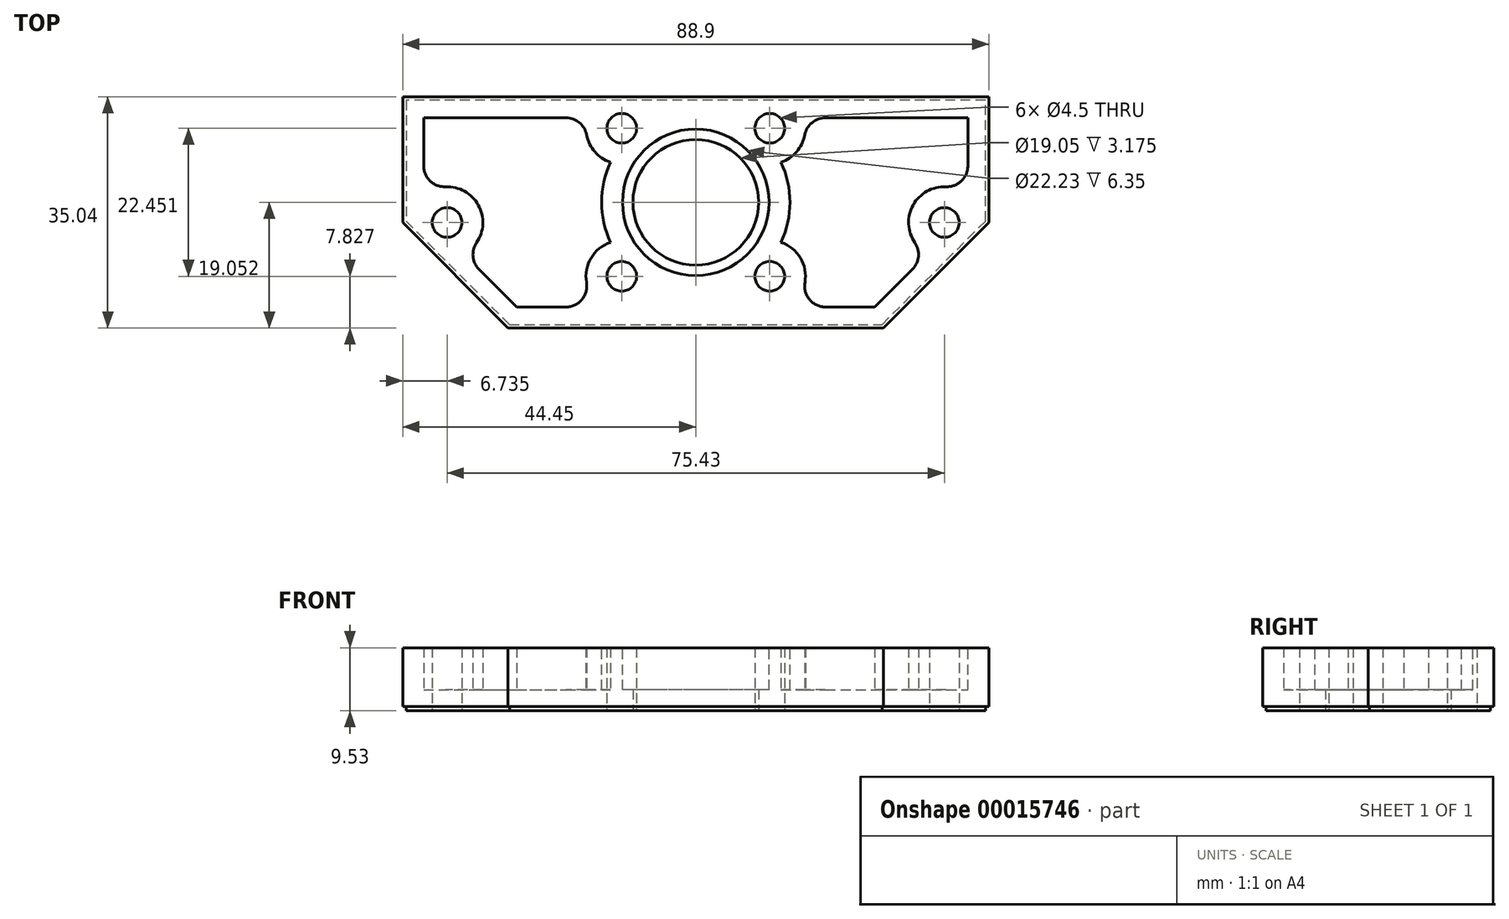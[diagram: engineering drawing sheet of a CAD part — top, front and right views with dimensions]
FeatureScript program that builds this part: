
annotation { "Feature Type Name" : "Feature", "Feature Type Description" : "" }
export const myFeature = defineFeature(function(context is Context, id is Id, definition is map)
    precondition{}
    {
        {
            var Q0;
            Q0=qCreatedBy(makeId("Top.planeOp"),FACE);
            var sketch = newSketch(context, id + "F0", { "sketchPlane" : qUnion([Q0])});
            skLineSegment(sketch, "E0.bottom", {"start": v(0, 0) * mm, "end": v(88.9, 0) * mm});
            skLineSegment(sketch, "E0.left", {"start": v(0, 0) * mm, "end": v(0, -19.05) * mm});
            skLineSegment(sketch, "E0.right", {"start": v(88.9, 0) * mm, "end": v(88.9, -19.05) * mm});
            skLineSegment(sketch, "E1", {"start": v(0, -19.05) * mm, "end": v(15.99, -35.04) * mm});
            skLineSegment(sketch, "E2", {"start": v(88.9, -19.05) * mm, "end": v(72.91, -35.04) * mm});
            skLineSegment(sketch, "E3", {"start": v(15.99, -35.04) * mm, "end": v(72.91, -35.04) * mm});
            skLineSegment(sketch, "E4", {"start": v(0, -19.05) * mm, "end": v(6.74, -19.05) * mm, "construction": true});
            skCircle(sketch, "E5", {"center": v(6.74, -19.05) * mm, "radius": 4.76 * mm, "construction": true});
            skLineSegment(sketch, "E6", {"start": v(88.9, -19.05) * mm, "end": v(82.16, -19.05) * mm, "construction": true});
            skLineSegment(sketch, "E7", {"start": v(44.45, -15.99) * mm, "end": v(44.45, -35.04) * mm, "construction": true});
            skCircle(sketch, "E8", {"center": v(44.45, -15.99) * mm, "radius": 9.53 * mm});
            skCircle(sketch, "E9", {"center": v(6.74, -19.05) * mm, "radius": 2.25 * mm});
            skCircle(sketch, "E10", {"center": v(82.16, -19.05) * mm, "radius": 2.25 * mm});
            skLineSegment(sketch, "E11.bottom", {"start": v(55.68, -27.21) * mm, "end": v(33.22, -27.21) * mm, "construction": true});
            skLineSegment(sketch, "E11.top", {"start": v(55.68, -4.76) * mm, "end": v(33.22, -4.76) * mm, "construction": true});
            skLineSegment(sketch, "E11.left", {"start": v(55.68, -27.21) * mm, "end": v(55.68, -4.76) * mm, "construction": true});
            skLineSegment(sketch, "E11.right", {"start": v(33.22, -27.21) * mm, "end": v(33.22, -4.76) * mm, "construction": true});
            skCircle(sketch, "E12", {"center": v(44.45, -15.99) * mm, "radius": 11.11 * mm, "construction": true});
            skCircle(sketch, "E13", {"center": v(55.68, -4.76) * mm, "radius": 4.76 * mm, "construction": true});
            skCircle(sketch, "E14", {"center": v(33.22, -4.76) * mm, "radius": 2.25 * mm});
            skCircle(sketch, "E15", {"center": v(55.68, -4.76) * mm, "radius": 2.25 * mm});
            skCircle(sketch, "E16", {"center": v(55.68, -27.21) * mm, "radius": 2.25 * mm});
            skCircle(sketch, "E17", {"center": v(33.22, -27.21) * mm, "radius": 2.25 * mm});
            skSolve(sketch);
        }
        {
            var Q0;
            Q0 = qSketchRegion(id + "F0", true);
            extrude(context, id + "F1", {"entities" : qUnion([Q0]), "depth" : 9.52 * mm});
        }
        {
            var Q0;
            Q0=makeQuery(id+"F1.opExtrude","CAP_FACE",FACE,{"disambiguationData":[OSD([sQuery(id+"F0.wireOp",EDGE,"E0.bottom"),sQuery(id+"F0.wireOp",EDGE,"E0.left"),sQuery(id+"F0.wireOp",EDGE,"E0.right"),sQuery(id+"F0.wireOp",EDGE,"E1"),sQuery(id+"F0.wireOp",EDGE,"E2"),sQuery(id+"F0.wireOp",EDGE,"E3"),sQuery(id+"F0.wireOp",EDGE,"E8"),sQuery(id+"F0.wireOp",EDGE,"E9"),sQuery(id+"F0.wireOp",EDGE,"E10"),sQuery(id+"F0.wireOp",EDGE,"E14"),sQuery(id+"F0.wireOp",EDGE,"E15"),sQuery(id+"F0.wireOp",EDGE,"E16"),sQuery(id+"F0.wireOp",EDGE,"E17")])],"isStart":false});
            var sketch = newSketch(context, id + "F2", { "sketchPlane" : qUnion([Q0])});
            skCircle(sketch, "E18", {"center": v(44.45, -15.99) * mm, "radius": 11.11 * mm});
            skSolve(sketch);
        }
        {
            var Q0;
            Q0 = qSketchRegion(id + "F2", true);
            extrude(context, id + "F3", {"entities" : qUnion([Q0]), "operationType" : NewBodyOperationType.REMOVE, "oppositeDirection" : true, "depth" : 6.35 * mm});
        }
        {
            var Q0;
            Q0=makeQuery(id+"F1.opExtrude","CAP_FACE",FACE,{"disambiguationData":[OSD([sQuery(id+"F0.wireOp",EDGE,"E0.bottom"),sQuery(id+"F0.wireOp",EDGE,"E0.left"),sQuery(id+"F0.wireOp",EDGE,"E0.right"),sQuery(id+"F0.wireOp",EDGE,"E1"),sQuery(id+"F0.wireOp",EDGE,"E2"),sQuery(id+"F0.wireOp",EDGE,"E3"),sQuery(id+"F0.wireOp",EDGE,"E8"),sQuery(id+"F0.wireOp",EDGE,"E9"),sQuery(id+"F0.wireOp",EDGE,"E10"),sQuery(id+"F0.wireOp",EDGE,"E14"),sQuery(id+"F0.wireOp",EDGE,"E15"),sQuery(id+"F0.wireOp",EDGE,"E16"),sQuery(id+"F0.wireOp",EDGE,"E17")])],"isStart":false});
            shell(context, id + "F4", {"entities" : qUnion([Q0]), "thickness" : 3.17 * mm});
        }
        {
            var Q0;
            Q0=makeQuery(id+"F4.opShell","OFFSET_FACE",FACE,{"disambiguationData":[OSD([sQuery(id+"F0.wireOp",EDGE,"E0.bottom"),sQuery(id+"F0.wireOp",EDGE,"E0.left"),sQuery(id+"F0.wireOp",EDGE,"E0.right"),sQuery(id+"F0.wireOp",EDGE,"E1"),sQuery(id+"F0.wireOp",EDGE,"E2"),sQuery(id+"F0.wireOp",EDGE,"E3"),sQuery(id+"F0.wireOp",EDGE,"E8"),sQuery(id+"F0.wireOp",EDGE,"E9"),sQuery(id+"F0.wireOp",EDGE,"E10"),sQuery(id+"F0.wireOp",EDGE,"E14"),sQuery(id+"F0.wireOp",EDGE,"E15"),sQuery(id+"F0.wireOp",EDGE,"E16"),sQuery(id+"F0.wireOp",EDGE,"E17")]),OD(0.0)]});
            var Q1;
            Q1=makeQuery(id+"F4.opShell","OFFSET_FACE",FACE,{"disambiguationData":[OSD([sQuery(id+"F0.wireOp",EDGE,"E0.bottom"),sQuery(id+"F0.wireOp",EDGE,"E0.left"),sQuery(id+"F0.wireOp",EDGE,"E0.right"),sQuery(id+"F0.wireOp",EDGE,"E1"),sQuery(id+"F0.wireOp",EDGE,"E2"),sQuery(id+"F0.wireOp",EDGE,"E3"),sQuery(id+"F0.wireOp",EDGE,"E8"),sQuery(id+"F0.wireOp",EDGE,"E9"),sQuery(id+"F0.wireOp",EDGE,"E10"),sQuery(id+"F0.wireOp",EDGE,"E14"),sQuery(id+"F0.wireOp",EDGE,"E15"),sQuery(id+"F0.wireOp",EDGE,"E16"),sQuery(id+"F0.wireOp",EDGE,"E17")]),OD(0.0)]});
            var Q2;
            Q2=makeQuery(id+"F1.opExtrude","CAP_FACE",FACE,{"disambiguationData":[OSD([sQuery(id+"F0.wireOp",EDGE,"E0.bottom"),sQuery(id+"F0.wireOp",EDGE,"E0.left"),sQuery(id+"F0.wireOp",EDGE,"E0.right"),sQuery(id+"F0.wireOp",EDGE,"E1"),sQuery(id+"F0.wireOp",EDGE,"E2"),sQuery(id+"F0.wireOp",EDGE,"E3"),sQuery(id+"F0.wireOp",EDGE,"E8"),sQuery(id+"F0.wireOp",EDGE,"E9"),sQuery(id+"F0.wireOp",EDGE,"E10"),sQuery(id+"F0.wireOp",EDGE,"E14"),sQuery(id+"F0.wireOp",EDGE,"E15"),sQuery(id+"F0.wireOp",EDGE,"E16"),sQuery(id+"F0.wireOp",EDGE,"E17")])],"isStart":false});
            extrude(context, id + "F5", {"entities" : qUnion([Q0, Q1]), "operationType" : NewBodyOperationType.ADD, "endBound" : BoundingType.UP_TO_SURFACE, "endBoundEntityFace" : qUnion([Q2]), "depth" : 25.4 * mm});
        }
        {
            var Q0;
            Q0=makeQuery(id+"F4.opShell","TWEAK_EDGE",EDGE,{"derivedFrom":[makeQuery(id+"F1.opExtrude","SWEPT_FACE",FACE,{"disambiguationData":[OSD([sQuery(id+"F0.wireOp",EDGE,"E0.left")])]}),makeQuery(id+"F1.opExtrude","SWEPT_FACE",FACE,{"disambiguationData":[OSD([sQuery(id+"F0.wireOp",EDGE,"E9")])]})]});
            var Q1;
            Q1=makeQuery(id+"F4.opShell","TWEAK_EDGE",EDGE,{"derivedFrom":[makeQuery(id+"F1.opExtrude","SWEPT_FACE",FACE,{"disambiguationData":[OSD([sQuery(id+"F0.wireOp",EDGE,"E1")])]}),makeQuery(id+"F1.opExtrude","SWEPT_FACE",FACE,{"disambiguationData":[OSD([sQuery(id+"F0.wireOp",EDGE,"E9")])]})]});
            var Q2;
            Q2=makeQuery(id+"F4.opShell","TWEAK_EDGE",EDGE,{"disambiguationData":[OD(0.0)],"derivedFrom":[makeQuery(id+"F1.opExtrude","SWEPT_FACE",FACE,{"disambiguationData":[OSD([sQuery(id+"F0.wireOp",EDGE,"E3")])]}),makeQuery(id+"F1.opExtrude","SWEPT_FACE",FACE,{"disambiguationData":[OSD([sQuery(id+"F0.wireOp",EDGE,"E17")])]})]});
            var Q3;
            Q3=makeQuery(id+"F4.opShell","TWEAK_EDGE",EDGE,{"disambiguationData":[OD(0.0)],"derivedFrom":[makeQuery(id+"F1.opExtrude","SWEPT_FACE",FACE,{"disambiguationData":[OSD([sQuery(id+"F0.wireOp",EDGE,"E0.bottom")])]}),makeQuery(id+"F1.opExtrude","SWEPT_FACE",FACE,{"disambiguationData":[OSD([sQuery(id+"F0.wireOp",EDGE,"E14")])]})]});
            var Q4;
            Q4=makeQuery(id+"F4.opShell","TWEAK_EDGE",EDGE,{"disambiguationData":[OD(0.0)],"derivedFrom":[makeQuery(id+"F1.opExtrude","SWEPT_FACE",FACE,{"disambiguationData":[OSD([sQuery(id+"F0.wireOp",EDGE,"E0.bottom")])]}),makeQuery(id+"F1.opExtrude","SWEPT_FACE",FACE,{"disambiguationData":[OSD([sQuery(id+"F0.wireOp",EDGE,"E15")])]})]});
            var Q5;
            Q5=makeQuery(id+"F4.opShell","TWEAK_EDGE",EDGE,{"disambiguationData":[OD(0.0)],"derivedFrom":[makeQuery(id+"F1.opExtrude","SWEPT_FACE",FACE,{"disambiguationData":[OSD([sQuery(id+"F0.wireOp",EDGE,"E3")])]}),makeQuery(id+"F1.opExtrude","SWEPT_FACE",FACE,{"disambiguationData":[OSD([sQuery(id+"F0.wireOp",EDGE,"E16")])]})]});
            var Q6;
            Q6=makeQuery(id+"F4.opShell","TWEAK_EDGE",EDGE,{"derivedFrom":[makeQuery(id+"F1.opExtrude","SWEPT_FACE",FACE,{"disambiguationData":[OSD([sQuery(id+"F0.wireOp",EDGE,"E2")])]}),makeQuery(id+"F1.opExtrude","SWEPT_FACE",FACE,{"disambiguationData":[OSD([sQuery(id+"F0.wireOp",EDGE,"E10")])]})]});
            var Q7;
            Q7=makeQuery(id+"F4.opShell","TWEAK_EDGE",EDGE,{"derivedFrom":[makeQuery(id+"F1.opExtrude","SWEPT_FACE",FACE,{"disambiguationData":[OSD([sQuery(id+"F0.wireOp",EDGE,"E0.right")])]}),makeQuery(id+"F1.opExtrude","SWEPT_FACE",FACE,{"disambiguationData":[OSD([sQuery(id+"F0.wireOp",EDGE,"E10")])]})]});
            fillet(context, id + "F6", {"entities" : qUnion([Q0, Q1, Q2, Q3, Q4, Q5, Q6, Q7]), "radius" : 3.17 * mm, "tangentPropagation" : true, "allowEdgeOverflow" : false});
        }
        {
            var Q0;
            Q0=makeQuery(id+"F1.opExtrude","SWEPT_FACE",FACE,{"disambiguationData":[OSD([sQuery(id+"F0.wireOp",EDGE,"E0.right")])]});
            var sketch = newSketch(context, id + "F7", { "sketchPlane" : qUnion([Q0])});
            skLineSegment(sketch, "E19.bottom", {"start": v(0, 0) * mm, "end": v(-0.5, 0) * mm});
            skLineSegment(sketch, "E19.top", {"start": v(0, 0.64) * mm, "end": v(-0.5, 0.64) * mm});
            skLineSegment(sketch, "E19.left", {"start": v(0, 0) * mm, "end": v(0, 0.64) * mm});
            skLineSegment(sketch, "E19.right", {"start": v(-0.5, 0) * mm, "end": v(-0.5, 0.64) * mm});
            skSolve(sketch);
        }
        {
            var Q0;
            Q0=makeQuery(id+"F7.imprint","IMPRINT",FACE,{"disambiguationData":[TD([[makeQuery(id+"F7.imprint","IMPRINT",EDGE,{"derivedFrom":sQuery(id+"F7.wireOp",EDGE,"E19.bottom")}),-1.0]])]});
            var Q1;
            Q1=makeQuery(id+"F1.opExtrude","CAP_EDGE",EDGE,{"disambiguationData":[OSD([sQuery(id+"F0.wireOp",EDGE,"E0.bottom")])],"isStart":true});
            var Q2;
            Q2=makeQuery(id+"F1.opExtrude","CAP_EDGE",EDGE,{"disambiguationData":[OSD([sQuery(id+"F0.wireOp",EDGE,"E0.left")])],"isStart":true});
            var Q3;
            Q3=makeQuery(id+"F1.opExtrude","CAP_EDGE",EDGE,{"disambiguationData":[OSD([sQuery(id+"F0.wireOp",EDGE,"E1")])],"isStart":true});
            var Q4;
            Q4=makeQuery(id+"F1.opExtrude","CAP_EDGE",EDGE,{"disambiguationData":[OSD([sQuery(id+"F0.wireOp",EDGE,"E3")])],"isStart":true});
            var Q5;
            Q5=makeQuery(id+"F1.opExtrude","CAP_EDGE",EDGE,{"disambiguationData":[OSD([sQuery(id+"F0.wireOp",EDGE,"E2")])],"isStart":true});
            var Q6;
            Q6=makeQuery(id+"F1.opExtrude","CAP_EDGE",EDGE,{"disambiguationData":[OSD([sQuery(id+"F0.wireOp",EDGE,"E0.right")])],"isStart":true});
            sweep(context, id + "F8", {"operationType" : NewBodyOperationType.REMOVE, "profiles" : qUnion([Q0]), "path" : qUnion([Q1, Q2, Q3, Q4, Q5, Q6])});
        }
    });
